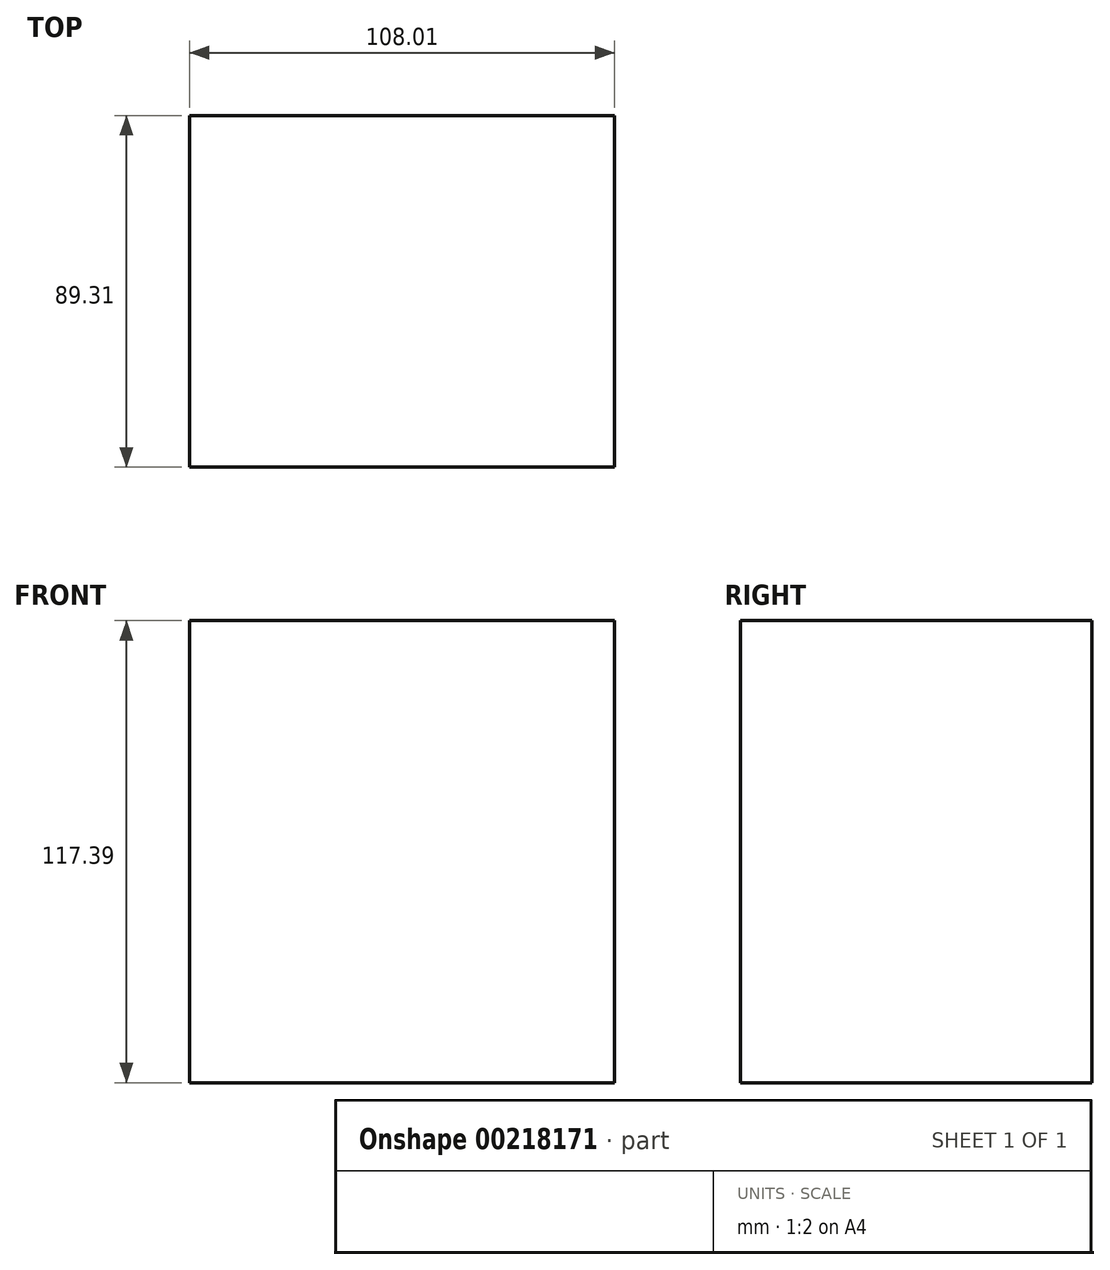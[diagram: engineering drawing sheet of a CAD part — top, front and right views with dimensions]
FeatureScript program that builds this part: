
annotation { "Feature Type Name" : "Feature", "Feature Type Description" : "" }
export const myFeature = defineFeature(function(context is Context, id is Id, definition is map)
    precondition{}
    {
        {
            var Q0;
            Q0=qCreatedBy(makeId("Top.planeOp"),FACE);
            var sketch = newSketch(context, id + "F0", { "sketchPlane" : qUnion([Q0])});
            skLineSegment(sketch, "E0.bottom", {"start": v(-52.95, 43.2) * mm, "end": v(55.06, 43.2) * mm});
            skLineSegment(sketch, "E0.top", {"start": v(-52.95, -46.1) * mm, "end": v(55.06, -46.1) * mm});
            skLineSegment(sketch, "E0.left", {"start": v(-52.95, 43.2) * mm, "end": v(-52.95, -46.1) * mm});
            skLineSegment(sketch, "E0.right", {"start": v(55.06, 43.2) * mm, "end": v(55.06, -46.1) * mm});
            skSolve(sketch);
        }
        {
            var Q0;
            Q0=makeQuery(id+"F0.imprint","IMPRINT",FACE,{"disambiguationData":[TD([[makeQuery(id+"F0.imprint","IMPRINT",EDGE,{"derivedFrom":sQuery(id+"F0.wireOp",EDGE,"E0.bottom")}),-1.0]])]});
            extrude(context, id + "F1", {"entities" : qUnion([Q0]), "oppositeDirection" : true, "depth" : 117.4 * mm});
        }
    });
